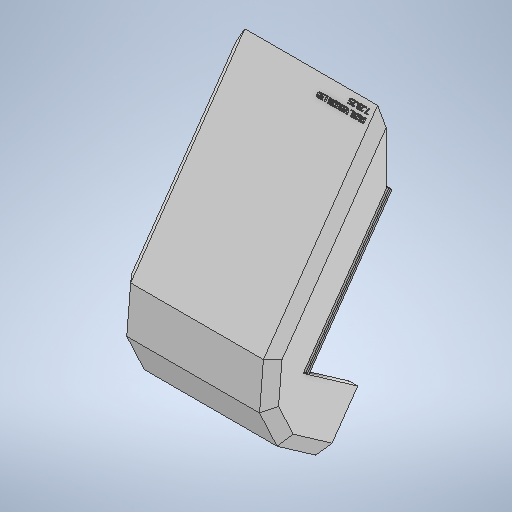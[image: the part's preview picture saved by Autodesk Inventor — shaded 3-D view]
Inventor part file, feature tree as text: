
AUTODESK INVENTOR PART (.ipt)
format: ipt  version: 2025.2 (Build 292293000, 293)  size: 1,263,104 bytes
history: native  units: in
note: dims shown in document units (in); Inventor stores cm internally (conversion verified against a paired STEP export)
features: sketch x43, extrude x39, projected_geometry x9, plane x8, move_body x1, chamfer x1, fillet x1, hole x1
ambient origin geometry x8: Origin, YZ Plane, XZ Plane, XY Plane, X Axis, Y Axis, Z Axis, Center Point
bodies: Solid1 (feature_tree)
feature tree (103):
  extrude  "Extrusion1"  Depth=0.1969in TaperAngle=0.0deg
  move_body  "Move Body1"
  plane  "Work Plane1"
  sketch  "Sketch5"  dims[d5=1.7717in d6=1.7717in d7=1.7717in d8=1.7717in d9=0.8108in d10=90.0deg d11=0.0787in d12=0.3701in d13=0.4252in d14=0.1362in d15=-0.0984in d16=-0.0591in d17=0.0in]
  plane  "Work Plane2"
  extrude  "Extrusion4"  TaperAngle=0.0deg  [1 undecoded]
  extrude  "Extrusion6"  Depth=0.2405in
  extrude  "Extrusion8"  Depth=2.5591in TaperAngle=0.0deg
  chamfer  "Chamfer1"  [1 undecoded]
  extrude  "Extrusion11"  Depth=0.2362in
  plane  "Work Plane3"
  plane  "Work Plane7"
  extrude  "Extrusion22"  Depth=0.1969in TaperAngle=0.0deg
  extrude  "Extrusion25"  Depth=0.5027in
  extrude  "Extrusion26"  Depth=0.5027in
  sketch  "Sketch33"  dims[d96=0.2362in d97=0.0in d100=3.6403in]
  extrude  "Extrusion27"  Depth=0.2362in TaperAngle=0.0deg
  extrude  "Extrusion28"  Depth=3.6403in
  sketch  "Sketch36"  dims[d123=0.9331in d124=0.9712in d125=0.0in]
  extrude  "Extrusion29"  Depth=1.9685in
  extrude  "Extrusion30"  Depth=0.1575in
  extrude  "Extrusion31"  Depth=0.9712in TaperAngle=0.0deg
  sketch  "Sketch39"  dims[d138=0.4331in d139=0.1181in d140=0.0in]
  extrude  "Extrusion32"  Depth=11.3469in TaperAngle=0.0deg
  fillet  "Fillet1"  Radius=11.3469in
  extrude  "Extrusion33"  Depth=0.4331in
  extrude  "Extrusion34"  Depth=0.1181in TaperAngle=0.0deg
  extrude  "Extrusion35"  Depth=0.0787in
  plane  "Work Plane8"
  sketch  "Sketch45"  dims[d160=0.1181in d161=0.0in d162=0.1969in d163=0.0in d164=0.1181in d165=0.0in]
  extrude  "Extrusion37"  Depth=0.2756in
  extrude  "Extrusion38"  Depth=0.1181in TaperAngle=0.0deg
  extrude  "Extrusion40"  Depth=0.5906in
  extrude  "Extrusion41"  Depth=0.1181in TaperAngle=0.0deg
  extrude  "Extrusion43"  Depth=4.7244in TaperAngle=0.0deg
  extrude  "Extrusion44"  Depth=0.7313in TaperAngle=0.0deg
  extrude  "Extrusion46"  TaperAngle=0.0deg  [1 undecoded]
  extrude  "Extrusion48"  Depth=1.1024in
  extrude  "Extrusion50"  Depth=0.0394in TaperAngle=0.0deg
  extrude  "Extrusion51"  Depth=5.8937in TaperAngle=0.0deg
  extrude  "Extrusion52"  Depth=0.0591in
  extrude  "Extrusion53"  Depth=0.0492in
  plane  "Work Plane9"
  extrude  "Extrusion55"  Depth=3.3754in TaperAngle=0.0deg
  extrude  "Extrusion56"  Depth=0.5917in TaperAngle=0.0deg
  plane  "Work Plane10"
  extrude  "Extrusion57"  TaperAngle=120.0deg  [1 undecoded]
  plane  "Work Plane11"
  extrude  "Extrusion58"  TaperAngle=0.0deg  [1 undecoded]
  extrude  "Extrusion59"  Depth=1.1811in TaperAngle=0.0deg
  extrude  "Extrusion60"  TaperAngle=0.0deg  [1 undecoded]
  extrude  "Extrusion61"  TaperAngle=0.0deg  [1 undecoded]
  extrude  "Extrusion62"  Depth=0.2362in TaperAngle=0.0deg
  extrude  "Extrusion63"  Depth=0.5118in TaperAngle=0.0deg
  extrude  "Extrusion64"  Depth=0.0394in TaperAngle=0.0deg
  sketch  "Sketch1"  dims[d1=0.5512in d2=0.1969in d3=0.0in]
  sketch  "Sketch6"  dims[d18=0.2749in d24=0.2405in]
  sketch  "Sketch8"  dims[d25=2.7559in d26=0.0in d29=2.5591in d30=0.0in d36=0.0in d37=0.0in]
  sketch  "Sketch12"  dims[d42=0.2362in d43=0.2362in]
  sketch  "Sketch15"  dims[d52=0.2362in d53=0.0787in d54=45.0deg d55=0.1969in d56=0.0in]
  sketch  "Sketch28"  dims[d76=0.5027in d77=0.5027in]
  sketch  "Sketch31"  dims[d78=0.5027in d79=0.5027in]
  sketch  "Sketch32"  dims[d83=0.0in d84=0.0in d94=0.2362in d95=0.0in]
  sketch  "Sketch34"  dims[d101=2.7717in d112=1.9685in]
  sketch  "Sketch35"  dims[d113=0.6299in d114=0.0in d115=0.1575in d117=0.1575in d121=1.9685in d122=0.7874in]
  sketch  "Sketch37"  dims[d126=0.5906in d127=0.0in d128=11.3469in d129=0.0in d130=11.3469in d131=0.0in]
  sketch  "Sketch38"  dims[d136=0.4331in d137=0.4331in]
  sketch  "Sketch40"  dims[d141=0.6299in d142=0.0787in]
  sketch  "Sketch41"  dims[d147=0.2756in d149=0.2756in]
  sketch  "Sketch42"  dims[d150=0.0in d151=0.0in d154=0.1181in d155=0.0in]
  sketch  "Sketch44"  dims[d156=0.1181in d157=0.0in d158=0.5906in]
  projected_geometry  "Projected Loop2"
  projected_geometry  "Projected Loop3"
  projected_geometry  "Projected Loop5"
  sketch  "Sketch47"  dims[d168=0.5906in d169=0.0in d170=4.7244in d171=0.0in]
  sketch  "Sketch49"  dims[d174=0.0in d175=0.0in d176=0.7313in d177=0.0in]
  sketch  "Sketch50"  dims[d186=0.0in d187=0.0in d188=0.0in d189=0.0in]
  sketch  "Sketch52"  dims[d194=0.0in d195=0.0in d196=1.1024in]
  sketch  "Sketch53"  dims[d197=0.5906in d200=0.0394in d201=0.0in]
  sketch  "Sketch56"  dims[d218=0.0in d219=0.0in d220=5.8937in d221=0.0in]
  sketch  "Sketch59"  dims[d226=0.0886in d227=0.0591in]
  sketch  "Sketch60"  dims[d228=0.0492in d229=0.0492in]
  sketch  "Sketch61"  dims[d230=0.0886in d231=3.3754in d232=0.0in]
  sketch  "Sketch62"  dims[d233=0.9963in d234=0.5917in d235=0.0in]
  sketch  "Sketch63"  dims[d236=2.0564in d238=120.0deg]
  projected_geometry  "Projected Loop8"
  sketch  "Sketch65"  dims[d241=1.378in d242=0.0in d243=0.0in d244=0.0in]
  projected_geometry  "Projected Loop9"
  sketch  "Sketch67"  dims[d245=120.0deg d246=1.1811in d247=0.0in]
  sketch  "Sketch68"  dims[d248=120.0deg d249=0.0in d250=0.0in]
  projected_geometry  "Projected Loop10"
  sketch  "Sketch69"  dims[d251=0.7874in d252=0.0in d253=0.0in d254=0.0in]
  sketch  "Sketch70"  dims[d255=0.2362in d256=0.0in d257=0.2362in d258=0.0in]
  projected_geometry  "Projected Loop11"
  sketch  "Sketch71"  dims[d259=0.2362in d260=0.5118in d261=0.0in]
  projected_geometry  "Projected Loop12"
  sketch  "Sketch72"  dims[d262=0.1082in d263=0.0394in d264=0.0in]
  sketch  "Sketch73"  dims[d38=0.0197in d39=0.0344in]
  sketch  "Sketch74"  dims[d57=0.0197in]
  projected_geometry  "Projected Loop13"
  sketch  "Sketch75"  dims[d58=0.0344in d59=0.0197in d60=0.0344in d81=0.0197in d82=0.0344in d159=0.0344in d178=0.0in d179=0.0in d180=0.0in d181=0.0in d202=0.0197in d203=0.0344in d222=0.0197in d223=0.0344in]
  sketch  "Sketch2"  dims[d4=0.315in]
  hole  "Hole1"  [1 undecoded]
note: 8 required parameter values undecoded (feature->parameter linkage not recoverable at this tier; creation-order binding heuristic only, values carry confidence <= 0.55)
